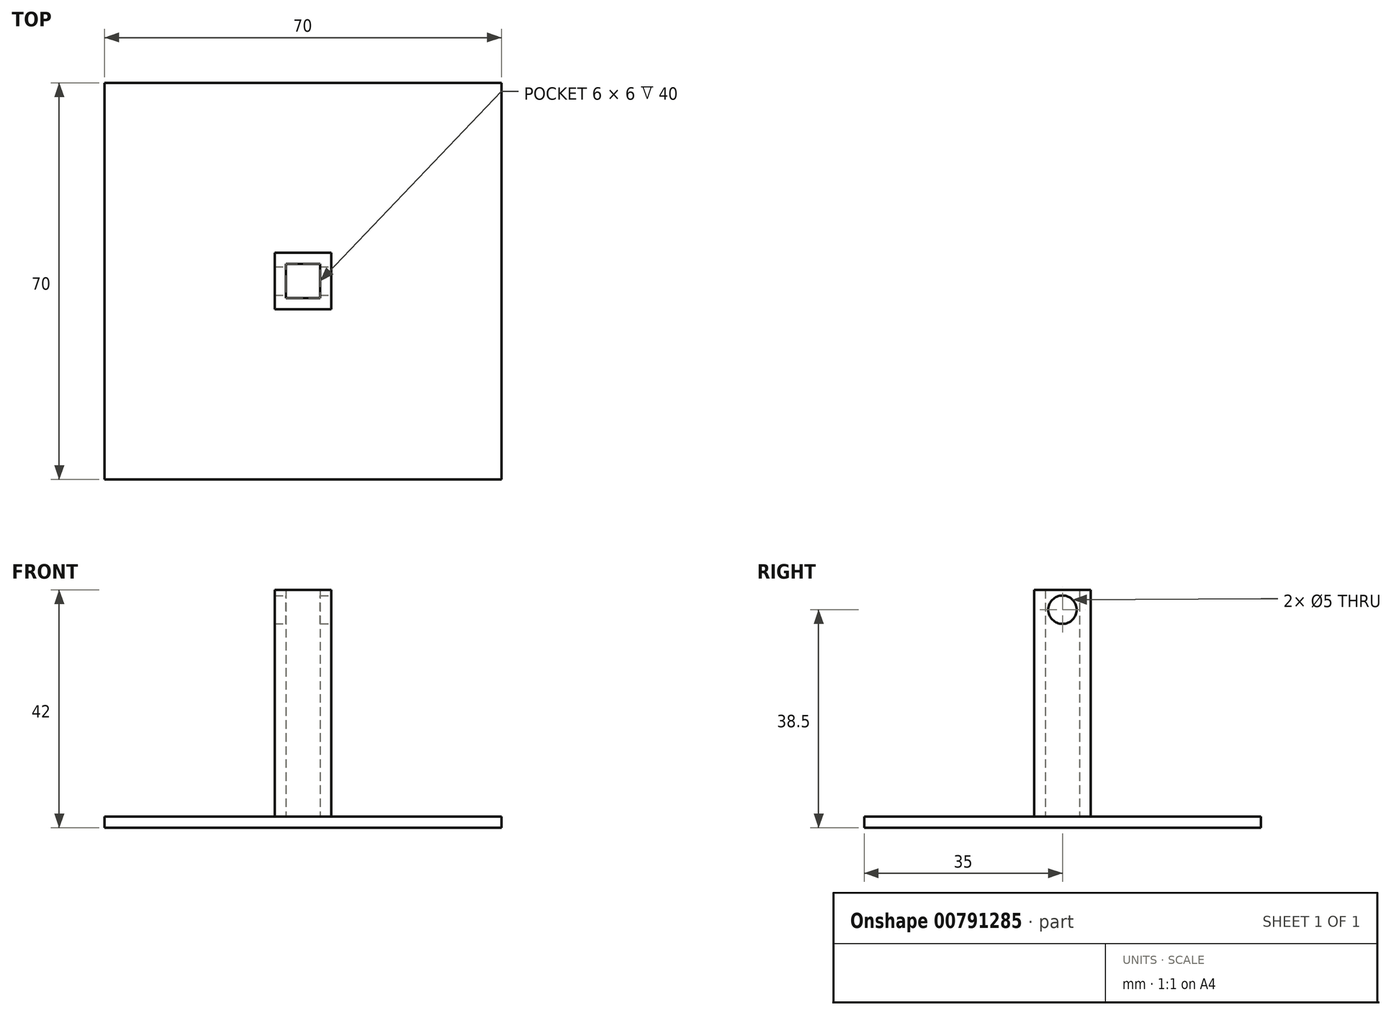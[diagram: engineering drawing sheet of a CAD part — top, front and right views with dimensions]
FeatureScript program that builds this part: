
annotation { "Feature Type Name" : "Feature", "Feature Type Description" : "" }
export const myFeature = defineFeature(function(context is Context, id is Id, definition is map)
    precondition{}
    {
        {
            var Q0;
            Q0=qCreatedBy(makeId("Top.planeOp"),FACE);
            var sketch = newSketch(context, id + "F0", { "sketchPlane" : qUnion([Q0])});
            skLineSegment(sketch, "E0.bottom", {"start": v(35, 35) * mm, "end": v(-35, 35) * mm});
            skLineSegment(sketch, "E0.top", {"start": v(35, -35) * mm, "end": v(-35, -35) * mm});
            skLineSegment(sketch, "E0.left", {"start": v(35, 35) * mm, "end": v(35, -35) * mm});
            skLineSegment(sketch, "E0.right", {"start": v(-35, 35) * mm, "end": v(-35, -35) * mm});
            skPoint(sketch, "E0.middle", {"position": v(0, 0) * mm});
            skLineSegment(sketch, "E1.bottom", {"start": v(5, 5) * mm, "end": v(-5, 5) * mm});
            skLineSegment(sketch, "E1.top", {"start": v(5, -5) * mm, "end": v(-5, -5) * mm});
            skLineSegment(sketch, "E1.left", {"start": v(5, 5) * mm, "end": v(5, -5) * mm});
            skLineSegment(sketch, "E1.right", {"start": v(-5, 5) * mm, "end": v(-5, -5) * mm});
            skLineSegment(sketch, "E2.bottom", {"start": v(3, 3) * mm, "end": v(-3, 3) * mm});
            skLineSegment(sketch, "E2.top", {"start": v(3, -3) * mm, "end": v(-3, -3) * mm});
            skLineSegment(sketch, "E2.left", {"start": v(3, 3) * mm, "end": v(3, -3) * mm});
            skLineSegment(sketch, "E2.right", {"start": v(-3, 3) * mm, "end": v(-3, -3) * mm});
            skSolve(sketch);
        }
        {
            var Q0;
            Q0=makeQuery(id+"F0.imprint","IMPRINT",FACE,{"disambiguationData":[TD([[makeQuery(id+"F0.imprint","IMPRINT",EDGE,{"derivedFrom":sQuery(id+"F0.wireOp",EDGE,"E0.bottom")}),1.0]])]});
            var Q1;
            Q1=makeQuery(id+"F0.imprint","IMPRINT",FACE,{"disambiguationData":[TD([[makeQuery(id+"F0.imprint","IMPRINT",EDGE,{"derivedFrom":sQuery(id+"F0.wireOp",EDGE,"E1.bottom")}),1.0]])]});
            var Q2;
            Q2=makeQuery(id+"F0.imprint","IMPRINT",FACE,{"disambiguationData":[TD([[makeQuery(id+"F0.imprint","IMPRINT",EDGE,{"derivedFrom":sQuery(id+"F0.wireOp",EDGE,"E2.bottom")}),1.0]])]});
            extrude(context, id + "F1", {"entities" : qUnion([Q0, Q1, Q2]), "depth" : 2 * mm, "offsetDistance" : 25 * mm});
        }
        {
            var Q0;
            Q0=makeQuery(id+"F0.imprint","IMPRINT",FACE,{"disambiguationData":[TD([[makeQuery(id+"F0.imprint","IMPRINT",EDGE,{"derivedFrom":sQuery(id+"F0.wireOp",EDGE,"E1.bottom")}),1.0]])]});
            extrude(context, id + "F2", {"entities" : qUnion([Q0]), "operationType" : NewBodyOperationType.ADD, "depth" : 35 * mm, "offsetDistance" : 25 * mm});
        }
        {
            var Q0;
            Q0=makeQuery(id+"F2.opExtrude","SWEPT_FACE",FACE,{"disambiguationData":[OSD([sQuery(id+"F0.wireOp",EDGE,"E1.left")])]});
            var sketch = newSketch(context, id + "F3", { "sketchPlane" : qUnion([Q0])});
            skLineSegment(sketch, "E3.bottom", {"start": v(-5, 35) * mm, "end": v(5, 35) * mm});
            skLineSegment(sketch, "E3.top", {"start": v(-5, 42) * mm, "end": v(5, 42) * mm});
            skLineSegment(sketch, "E3.left", {"start": v(-5, 35) * mm, "end": v(-5, 42) * mm});
            skLineSegment(sketch, "E3.right", {"start": v(5, 35) * mm, "end": v(5, 42) * mm});
            skLineSegment(sketch, "E4", {"start": v(0, 42) * mm, "end": v(0, 35) * mm});
            skCircle(sketch, "E5", {"center": v(0, 38.5) * mm, "radius": 2.5 * mm});
            skSolve(sketch);
        }
        {
            var Q0;
            Q0=makeQuery(id+"F3.imprint","IMPRINT",FACE,{"disambiguationData":[TD([[makeQuery(id+"F3.imprint","IMPRINT",EDGE,{"derivedFrom":sQuery(id+"F3.wireOp",EDGE,"E3.bottom")}),-1.0]])]});
            extrude(context, id + "F4", {"entities" : qUnion([Q0]), "operationType" : NewBodyOperationType.ADD, "oppositeDirection" : true, "depth" : 10 * mm, "offsetDistance" : 25 * mm});
        }
        {
            var Q0;
            Q0=makeQuery(id+"F4.opExtrude","SWEPT_FACE",FACE,{"disambiguationData":[OSD([sQuery(id+"F3.wireOp",EDGE,"E3.top")])]});
            var sketch = newSketch(context, id + "F5", { "sketchPlane" : qUnion([Q0])});
            skLineSegment(sketch, "E6.bottom", {"start": v(-5, -5) * mm, "end": v(5, -5) * mm});
            skLineSegment(sketch, "E6.top", {"start": v(-5, -3) * mm, "end": v(5, -3) * mm});
            skLineSegment(sketch, "E6.left", {"start": v(-5, -5) * mm, "end": v(-5, -3) * mm});
            skLineSegment(sketch, "E6.right", {"start": v(5, -5) * mm, "end": v(5, -3) * mm});
            skLineSegment(sketch, "E7.bottom", {"start": v(-5, 3) * mm, "end": v(5, 3) * mm});
            skLineSegment(sketch, "E7.top", {"start": v(-5, 5) * mm, "end": v(5, 5) * mm});
            skLineSegment(sketch, "E7.left", {"start": v(-5, 3) * mm, "end": v(-5, 5) * mm});
            skLineSegment(sketch, "E7.right", {"start": v(5, 3) * mm, "end": v(5, 5) * mm});
            skLineSegment(sketch, "E8.bottom", {"start": v(-3, -5) * mm, "end": v(3, -5) * mm});
            skLineSegment(sketch, "E8.top", {"start": v(-3, 5) * mm, "end": v(3, 5) * mm});
            skLineSegment(sketch, "E8.left", {"start": v(-3, -5) * mm, "end": v(-3, 5) * mm});
            skLineSegment(sketch, "E8.right", {"start": v(3, -5) * mm, "end": v(3, 5) * mm});
            skSolve(sketch);
        }
        {
            var Q0;
            {var subQ5=sQuery(id+"F5.wireOp",EDGE,"E8.bottom");Q0=makeQuery(id+"F5.imprint","IMPRINT",FACE,{"disambiguationData":[TD([[makeQuery(id+"F5.imprint","IMPRINT",EDGE,{"derivedFrom":subQ5}),1.0]])]});}
            var Q1;
            {var subQ0=sQuery(id+"F5.wireOp",EDGE,"E8.left");var subQ1=sQuery(id+"F5.wireOp",EDGE,"E6.top");var subQ2=makeQuery(id+"F5.imprint","INTERSECT",VERTEX,{"derivedFrom":[subQ1,subQ0]});Q1=makeQuery(id+"F5.imprint","IMPRINT",FACE,{"disambiguationData":[TD([[makeQuery(id+"F5.imprint","IMPRINT",EDGE,{"disambiguationData":[TD([[subQ2,-1.0]])],"derivedFrom":subQ1}),1.0]])]});}
            var Q2;
            {var subQ5=sQuery(id+"F5.wireOp",EDGE,"E8.top");Q2=makeQuery(id+"F5.imprint","IMPRINT",FACE,{"disambiguationData":[TD([[makeQuery(id+"F5.imprint","IMPRINT",EDGE,{"derivedFrom":subQ5}),-1.0]])]});}
            extrude(context, id + "F6", {"entities" : qUnion([Q0, Q1, Q2]), "operationType" : NewBodyOperationType.REMOVE, "oppositeDirection" : true, "depth" : 7 * mm, "offsetDistance" : 25 * mm});
        }
    });
